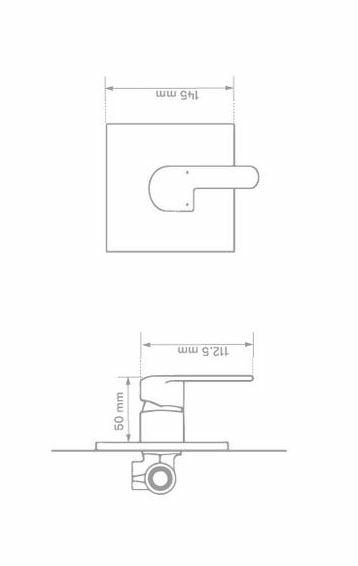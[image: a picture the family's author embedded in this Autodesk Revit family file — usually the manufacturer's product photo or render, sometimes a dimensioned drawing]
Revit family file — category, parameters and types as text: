
# Revit family: 01-1528-11 MEZCLADOR LAVAPLATOS 8 COLECCION PIANA
name_source: partatom
category: Plumbing Fixtures
revit_build: Autodesk Revit 2018 (Build: 20170223_1515(x64)
units: mm (PartAtom-declared; Revit-internal decimal feet)

## family parameters
Cut with Voids When Loaded = No
Host = Face
OmniClass Number = 23.31.11.00
Part Type = Normal
Room Calculation Point = No
Round Connector Dimension = Use Diameter
Shared = No

## types (1)
- 01-1528-11
    Alto Aireador = 201 mm
    Alto brazo = 265 mm  [stored 0.869423 ft]
    Ancho brazo = 164 mm
    Ancho entre manijas = 203.2 mm  [stored 0.666667 ft]
    Ancho manija = 75 mm
    CW Connection = Yes
    Default Elevation = 0 mm  [stored 0 ft]
    Description = Bimando
    HW Connection = Yes
    Link Ficha Tecnica = http://infotecnica.gricol.com
    Manufacturer = Gricol
    Model = 01-1528-11
    Plástico - ABS Cromado = Plastico ABS Cromado
    Product Name = MEZCLADOR LAVAPLATOS 8° COLECCION PIANA
    Type Image = <None>
    URL = https://www.gricol.com
    Vent Connection = No
    Waste Connection = No

note: [stored X ft] marks values corroborated as IEEE doubles in the binary element streams (Revit-internal decimal feet)

## geometry (parser evidence)
native form markers: Blend x2, Sweep x1
no freeform markers — native parametric forms only
